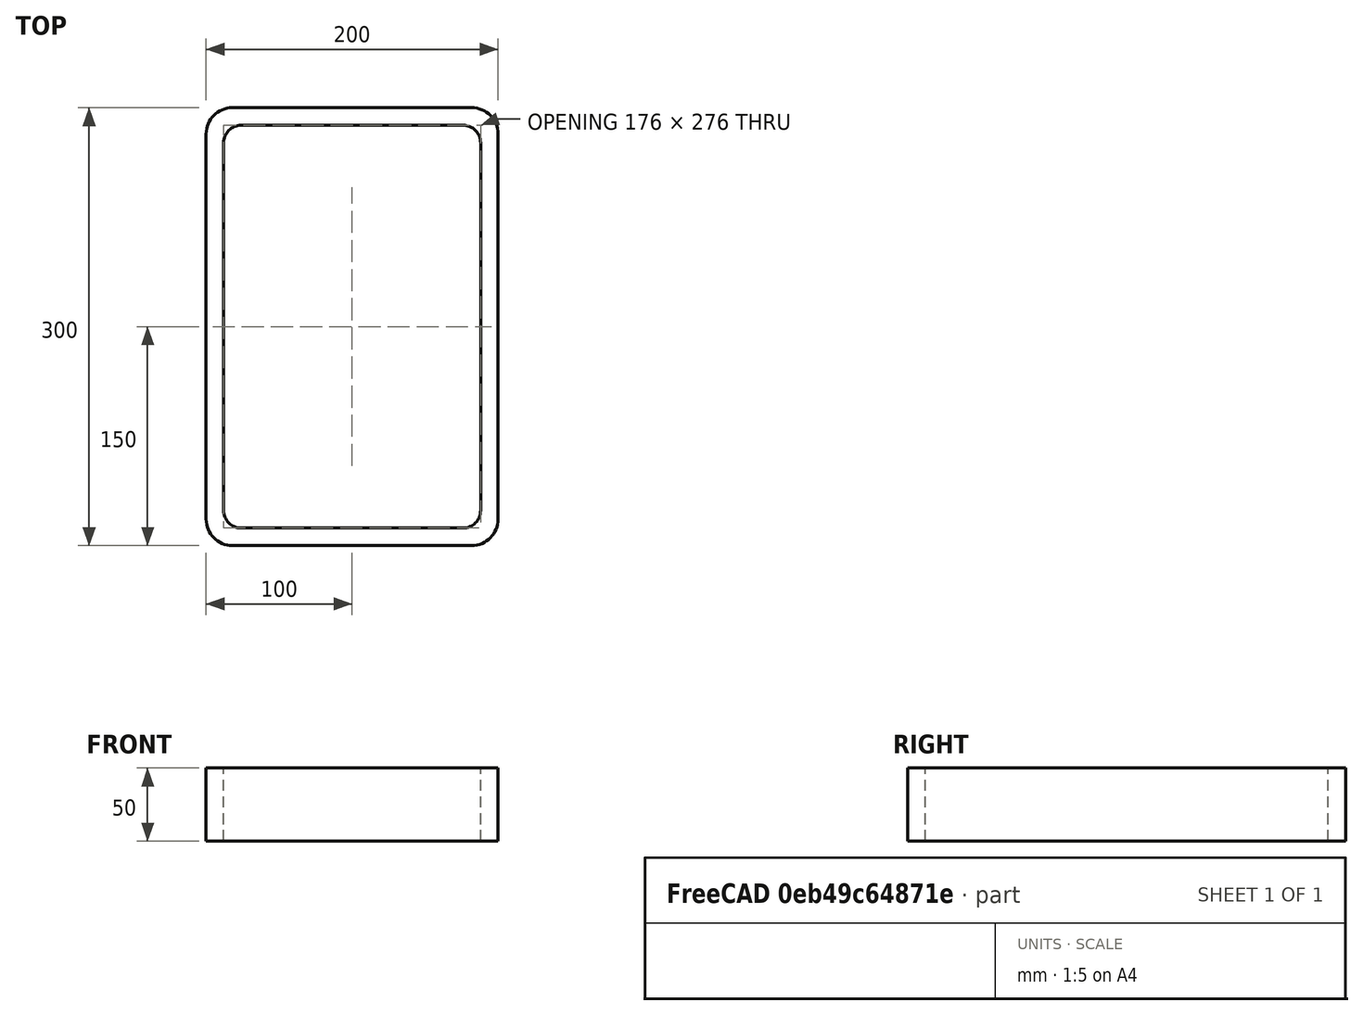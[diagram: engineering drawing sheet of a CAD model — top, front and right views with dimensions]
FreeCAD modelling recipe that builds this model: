
FCSTD DOCUMENT  (FreeCAD 0.15R4671 (Git))
Label: Rectangular hollow section 300x200x12 EN10219 S235JRH
License: All rights reserved
LicenseURL: http://en.wikipedia.org/wiki/All_rights_reserved
objects: Sketcher::SketchObject×1, Part::Extrusion×1
note: 2 computed .brp shape members not serialized (recipe doc carries the construction recipe); baked Part::Feature solids carry a one-line shape summary decoded from their .brp

FEATURE [Sketcher::SketchObject] Sketch
  sketch-geometry (16):
    g0: LineSegment StartX=-76 StartY=138 StartZ=0 EndX=76 EndY=138 EndZ=0
    g1: LineSegment StartX=88 StartY=126 StartZ=0 EndX=88 EndY=-126 EndZ=0
    g2: LineSegment StartX=76 StartY=-138 StartZ=0 EndX=-76 EndY=-138 EndZ=0
    g3: LineSegment StartX=-88 StartY=-126 StartZ=0 EndX=-88 EndY=126 EndZ=0
    g4: LineSegment StartX=-82 StartY=150 StartZ=0 EndX=82 EndY=150 EndZ=0
    g5: LineSegment StartX=100 StartY=132 StartZ=0 EndX=100 EndY=-132 EndZ=0
    g6: LineSegment StartX=82 StartY=-150 StartZ=0 EndX=-82 EndY=-150 EndZ=0
    g7: LineSegment StartX=-100 StartY=-132 StartZ=0 EndX=-100 EndY=132 EndZ=0
    g8: ArcOfCircle CenterX=-76 CenterY=126 CenterZ=0 NormalX=0 NormalY=0 NormalZ=1 Radius=12 StartAngle=1.5708 EndAngle=3.14159
    g9: ArcOfCircle CenterX=76 CenterY=126 CenterZ=0 NormalX=0 NormalY=0 NormalZ=1 Radius=12 StartAngle=0 EndAngle=1.5708
    g10: ArcOfCircle CenterX=76 CenterY=-126 CenterZ=0 NormalX=0 NormalY=0 NormalZ=1 Radius=12 StartAngle=4.71239 EndAngle=6.28319
    g11: ArcOfCircle CenterX=-76 CenterY=-126 CenterZ=0 NormalX=0 NormalY=0 NormalZ=1 Radius=12 StartAngle=3.14159 EndAngle=4.71239
    g12: ArcOfCircle CenterX=82 CenterY=132 CenterZ=0 NormalX=0 NormalY=0 NormalZ=1 Radius=18 StartAngle=0 EndAngle=1.5708
    g13: ArcOfCircle CenterX=82 CenterY=-132 CenterZ=0 NormalX=0 NormalY=0 NormalZ=1 Radius=18 StartAngle=4.71239 EndAngle=6.28319
    g14: ArcOfCircle CenterX=-82 CenterY=-132 CenterZ=0 NormalX=0 NormalY=0 NormalZ=1 Radius=18 StartAngle=3.14159 EndAngle=4.71239
    g15: ArcOfCircle CenterX=-82 CenterY=132 CenterZ=0 NormalX=0 NormalY=0 NormalZ=1 Radius=18 StartAngle=1.5708 EndAngle=3.14159
  constraints (36):
    c: Horizontal(g2)
    c: Vertical(g3)
    c: Horizontal(g6)
    c: Vertical(g7)
    c: Tangent(g3,g8) = 1.5708
    c: Tangent(g0,g8) = 1.5708
    c: Tangent(g0,g9) = 1.5708
    c: Tangent(g1,g9) = 1.5708
    c: Tangent(g1,g10) = 1.5708
    c: Tangent(g2,g10) = 1.5708
    c: Tangent(g2,g11) = 1.5708
    c: Tangent(g3,g11) = 1.5708
    c: Tangent(g4,g12) = 1.5708
    c: Tangent(g5,g12) = 1.5708
    c: Tangent(g5,g13) = 1.5708
    c: Tangent(g6,g13) = 1.5708
    c: Tangent(g6,g14) = 1.5708
    c: Tangent(g7,g14) = 1.5708
    c: Tangent(g7,g15) = 1.5708
    c: Tangent(g4,g15) = 1.5708
    c: Equal(g9,g8)
    c: Equal(g9,g11)
    c: Equal(g9,g10)
    c: Equal(g12,g15)
    c: Equal(g12,g14)
    c: Equal(g12,g13)
    c: Symmetric(g4,g6,g-1)
    c: Symmetric(g7,g5,g-2)
    c: DistanceY(g4,g6) = -300
    c: DistanceX(g7,g5) = 200
    c: Symmetric(g3,g1,g-2)
    c: Symmetric(g0,g2,g-1)
    c: DistanceY(g0,g4) = 12
    c: DistanceX(g5,g1) = -12
    c: Radius(g9) = 12
    c: Radius(g12) = 18
FEATURE [Part::Extrusion] Extrude  label="Rectangular hollow section 300x200x12 EN10219 S235JRH"
  Base = -> Sketch
  Dir = (0,0,50)
  Solid = true
